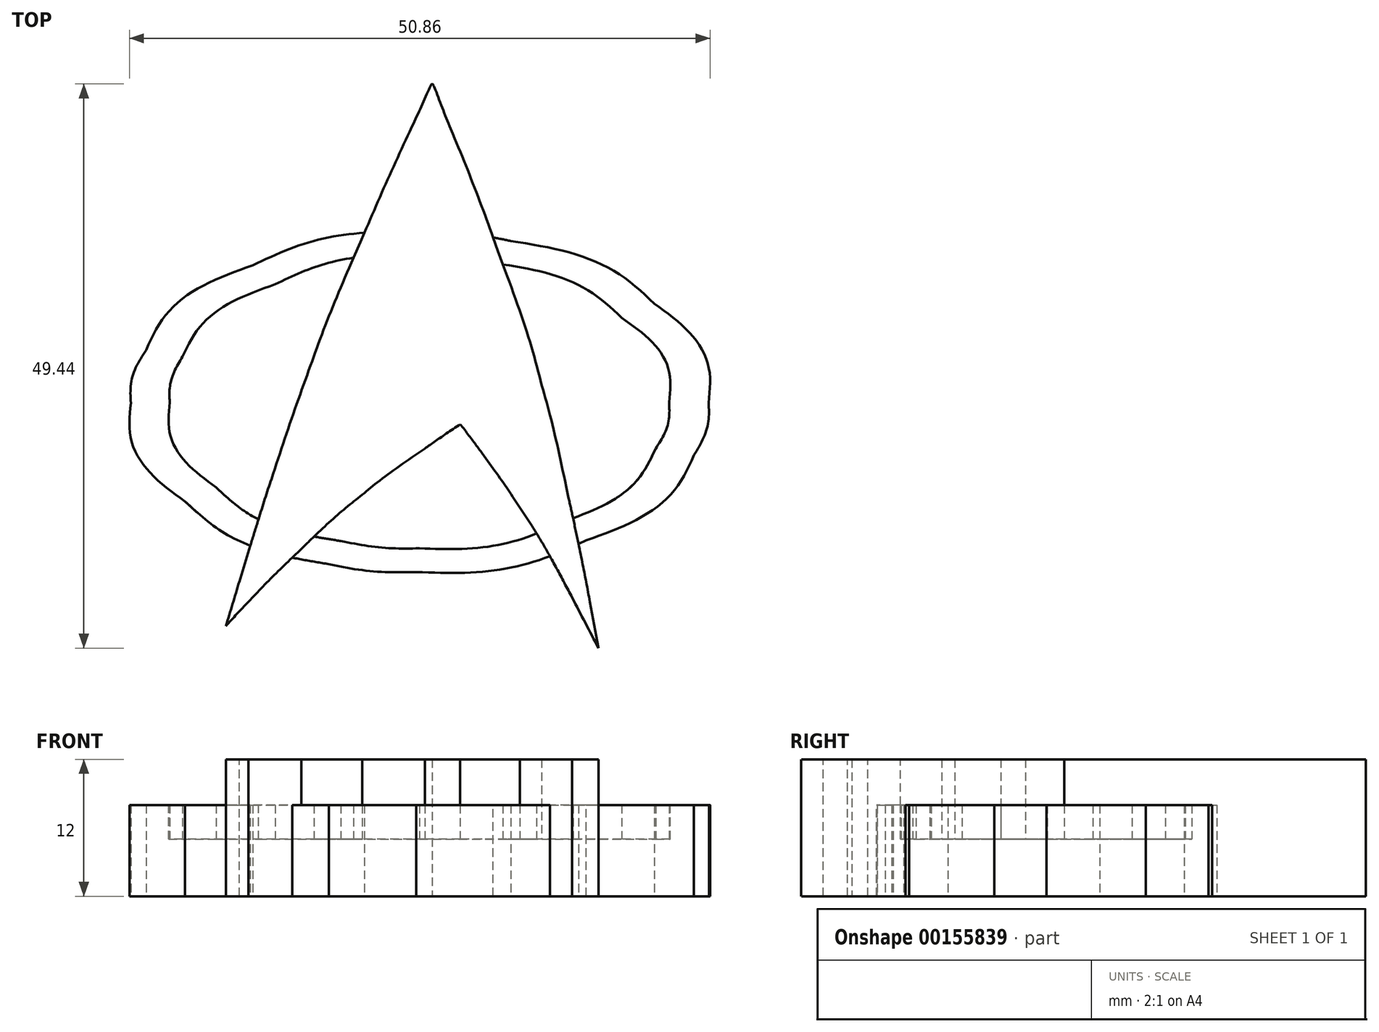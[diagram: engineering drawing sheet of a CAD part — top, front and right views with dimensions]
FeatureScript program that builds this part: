
annotation { "Feature Type Name" : "Feature", "Feature Type Description" : "" }
export const myFeature = defineFeature(function(context is Context, id is Id, definition is map)
    precondition{}
    {
        {
            var Q0;
            Q0=qCreatedBy(makeId("Top.planeOp"),FACE);
            var sketch = newSketch(context, id + "F0", { "sketchPlane" : qUnion([Q0])});
            skFitSpline(sketch, "E0", {"points": [v(14.01, -24.64) * mm, v(13.05, -22.8) * mm, v(12.29, -21.32) * mm, v(11.72, -20.22) * mm]});
            skFitSpline(sketch, "E1", {"points": [v(11.72, -20.22) * mm, v(9.94, -16.9) * mm, v(8.41, -14.28) * mm, v(7.13, -12.32) * mm]});
            skFitSpline(sketch, "E2", {"points": [v(7.13, -12.32) * mm, v(6.24, -10.97) * mm, v(5.14, -9.39) * mm, v(3.83, -7.58) * mm]});
            skFitSpline(sketch, "E3", {"points": [v(3.83, -7.58) * mm, v(3.36, -6.94) * mm, v(2.72, -6.08) * mm, v(1.9, -5.02) * mm]});
            skFitSpline(sketch, "E4", {"points": [v(1.9, -5.02) * mm, v(0.6, -5.9) * mm, v(-0.44, -6.62) * mm, v(-1.19, -7.15) * mm]});
            skFitSpline(sketch, "E5", {"points": [v(-1.19, -7.15) * mm, v(-3.64, -8.86) * mm, v(-5.47, -10.2) * mm, v(-6.68, -11.2) * mm]});
            skFitSpline(sketch, "E6", {"points": [v(-6.68, -11.2) * mm, v(-8.32, -12.52) * mm, v(-10.1, -14.1) * mm, v(-12.01, -15.95) * mm]});
            skFitSpline(sketch, "E7", {"points": [v(-12.01, -15.95) * mm, v(-13.68, -17.55) * mm, v(-15.23, -19.1) * mm, v(-16.65, -20.59) * mm]});
            skFitSpline(sketch, "E8", {"points": [v(-16.65, -20.59) * mm, v(-17.33, -21.3) * mm, v(-17.99, -22.01) * mm, v(-18.63, -22.72) * mm]});
            skFitSpline(sketch, "E9", {"points": [v(-18.63, -22.72) * mm, v(-18.24, -21.44) * mm, v(-17.84, -20.15) * mm, v(-17.45, -18.83) * mm]});
            skFitSpline(sketch, "E10", {"points": [v(-17.45, -18.83) * mm, v(-16.17, -14.67) * mm, v(-15.23, -11.67) * mm, v(-14.63, -9.82) * mm]});
            skFitSpline(sketch, "E11", {"points": [v(-14.63, -9.82) * mm, v(-13.49, -6.37) * mm, v(-12.35, -3.06) * mm, v(-11.21, 0.1) * mm]});
            skFitSpline(sketch, "E12", {"points": [v(-11.21, 0.1) * mm, v(-10.04, 3.3) * mm, v(-8.58, 6.91) * mm, v(-6.84, 10.93) * mm]});
            skFitSpline(sketch, "E13", {"points": [v(-6.84, 10.93) * mm, v(-5.42, 14.24) * mm, v(-3.98, 17.47) * mm, v(-2.52, 20.64) * mm]});
            skFitSpline(sketch, "E14", {"points": [v(-2.52, 20.64) * mm, v(-1.24, 23.41) * mm, v(-0.58, 24.8) * mm, v(-0.55, 24.8) * mm]});
            skFitSpline(sketch, "E15", {"points": [v(-0.55, 24.8) * mm, v(-0.51, 24.8) * mm, v(0.1, 23.34) * mm, v(1.27, 20.42) * mm]});
            skFitSpline(sketch, "E16", {"points": [v(1.27, 20.42) * mm, v(2.65, 17.01) * mm, v(3.97, 13.6) * mm, v(5.21, 10.18) * mm]});
            skFitSpline(sketch, "E17", {"points": [v(5.21, 10.18) * mm, v(6.92, 5.5) * mm, v(8.2, 1.56) * mm, v(9.05, -1.6) * mm]});
            skFitSpline(sketch, "E18", {"points": [v(9.05, -1.6) * mm, v(9.76, -4.2) * mm, v(10.55, -7.49) * mm, v(11.4, -11.47) * mm]});
            skFitSpline(sketch, "E19", {"points": [v(11.4, -11.47) * mm, v(12.11, -14.74) * mm, v(12.73, -17.78) * mm, v(13.27, -20.59) * mm]});
            skFitSpline(sketch, "E20", {"points": [v(13.27, -20.59) * mm, v(13.52, -21.94) * mm, v(13.76, -23.3) * mm, v(14.01, -24.64) * mm]});
            skFitSpline(sketch, "E21", {"points": [v(22.39, -7.74) * mm, v(20.64, -10.83) * mm, v(17.5, -13.32) * mm, v(12.95, -15.2) * mm]});
            skFitSpline(sketch, "E22", {"points": [v(12.95, -15.2) * mm, v(8.43, -17.05) * mm, v(3.47, -17.98) * mm, v(-1.93, -17.98) * mm]});
            skFitSpline(sketch, "E23", {"points": [v(-1.93, -17.98) * mm, v(-4.6, -17.98) * mm, v(-7.16, -17.75) * mm, v(-9.61, -17.28) * mm]});
            skFitSpline(sketch, "E24", {"points": [v(-9.61, -17.28) * mm, v(-14.84, -16.22) * mm, v(-19.04, -14.39) * mm, v(-22.2, -11.79) * mm]});
            skFitSpline(sketch, "E25", {"points": [v(-22.2, -11.79) * mm, v(-25.36, -9.16) * mm, v(-26.95, -6.28) * mm, v(-26.95, -3.15) * mm]});
            skFitSpline(sketch, "E26", {"points": [v(-26.95, -3.15) * mm, v(-26.95, -1.59) * mm, v(-26.5, -0.04) * mm, v(-25.61, 1.5) * mm]});
            skFitSpline(sketch, "E27", {"points": [v(-25.61, 1.5) * mm, v(-23.87, 4.58) * mm, v(-20.76, 7.05) * mm, v(-16.28, 8.9) * mm]});
            skFitSpline(sketch, "E28", {"points": [v(-16.28, 8.9) * mm, v(-11.8, 10.79) * mm, v(-6.86, 11.73) * mm, v(-1.45, 11.73) * mm]});
            skFitSpline(sketch, "E29", {"points": [v(-1.45, 11.73) * mm, v(1.28, 11.73) * mm, v(3.88, 11.5) * mm, v(6.33, 11.04) * mm]});
            skFitSpline(sketch, "E30", {"points": [v(6.33, 11.04) * mm, v(11.56, 10) * mm, v(15.76, 8.17) * mm, v(18.92, 5.54) * mm]});
            skFitSpline(sketch, "E31", {"points": [v(18.92, 5.54) * mm, v(22.08, 2.91) * mm, v(23.67, 0.01) * mm, v(23.67, -3.15) * mm]});
            skFitSpline(sketch, "E32", {"points": [v(23.67, -3.15) * mm, v(23.67, -4.64) * mm, v(23.24, -6.17) * mm, v(22.39, -7.74) * mm]});
            skFitSpline(sketch, "E33", {"points": [v(19.03, -7.15) * mm, v(19.8, -5.83) * mm, v(20.2, -4.48) * mm, v(20.2, -3.1) * mm]});
            skFitSpline(sketch, "E34", {"points": [v(20.2, -3.1) * mm, v(20.2, -0.4) * mm, v(18.81, 2.08) * mm, v(16.04, 4.32) * mm]});
            skFitSpline(sketch, "E35", {"points": [v(16.04, 4.32) * mm, v(13.3, 6.6) * mm, v(9.68, 8.17) * mm, v(5.16, 9.06) * mm]});
            skFitSpline(sketch, "E36", {"points": [v(5.16, 9.06) * mm, v(2.92, 9.5) * mm, v(0.66, 9.7) * mm, v(-1.61, 9.7) * mm]});
            skFitSpline(sketch, "E37", {"points": [v(-1.61, 9.7) * mm, v(-6.2, 9.7) * mm, v(-10.43, 8.89) * mm, v(-14.3, 7.25) * mm]});
            skFitSpline(sketch, "E38", {"points": [v(-14.3, 7.25) * mm, v(-18.18, 5.65) * mm, v(-20.88, 3.53) * mm, v(-22.41, 0.9) * mm]});
            skFitSpline(sketch, "E39", {"points": [v(-22.41, 0.9) * mm, v(-23.16, -0.45) * mm, v(-23.53, -1.78) * mm, v(-23.53, -3.1) * mm]});
            skFitSpline(sketch, "E40", {"points": [v(-23.53, -3.1) * mm, v(-23.53, -5.8) * mm, v(-22.18, -8.29) * mm, v(-19.48, -10.56) * mm]});
            skFitSpline(sketch, "E41", {"points": [v(-19.48, -10.56) * mm, v(-16.74, -12.8) * mm, v(-13.1, -14.37) * mm, v(-8.55, -15.26) * mm]});
            skFitSpline(sketch, "E42", {"points": [v(-8.55, -15.26) * mm, v(-6.24, -15.68) * mm, v(-3.94, -15.9) * mm, v(-1.67, -15.9) * mm]});
            skFitSpline(sketch, "E43", {"points": [v(-1.67, -15.9) * mm, v(2.96, -15.9) * mm, v(7.17, -15.11) * mm, v(10.97, -13.55) * mm]});
            skFitSpline(sketch, "E44", {"points": [v(10.97, -13.55) * mm, v(14.81, -11.95) * mm, v(17.5, -9.82) * mm, v(19.03, -7.15) * mm]});
            skSolve(sketch);
        }
        {
            var Q0;
            {var subQ4=sQuery(id+"F0.wireOp",EDGE,"E14");Q0=makeQuery(id+"F0.imprint","IMPRINT",FACE,{"disambiguationData":[TD([[makeQuery(id+"F0.imprint","IMPRINT",EDGE,{"derivedFrom":subQ4}),-1.0]])]});}
            var Q1;
            {var subQ12=sQuery(id+"F0.wireOp",EDGE,"E36");Q1=makeQuery(id+"F0.imprint","IMPRINT",FACE,{"disambiguationData":[TD([[makeQuery(id+"F0.imprint","IMPRINT",EDGE,{"derivedFrom":subQ12}),-1.0]])]});}
            var Q2;
            {var subQ17=sQuery(id+"F0.wireOp",EDGE,"E2");Q2=makeQuery(id+"F0.imprint","IMPRINT",FACE,{"disambiguationData":[TD([[makeQuery(id+"F0.imprint","IMPRINT",EDGE,{"derivedFrom":subQ17}),-1.0]])]});}
            var Q3;
            {var subQ1=sQuery(id+"F0.wireOp",EDGE,"E7");var subQ7=sQuery(id+"F0.wireOp",EDGE,"E6");var subQ8=makeQuery(id+"F0.imprint","INTERSECT",VERTEX,{"derivedFrom":[subQ7,subQ1]});Q3=makeQuery(id+"F0.imprint","IMPRINT",FACE,{"disambiguationData":[TD([[makeQuery(id+"F0.imprint","IMPRINT",EDGE,{"disambiguationData":[TD([[subQ8,1.0]])],"derivedFrom":subQ7}),-1.0]])]});}
            var Q4;
            {var subQ6=sQuery(id+"F0.wireOp",EDGE,"E8");Q4=makeQuery(id+"F0.imprint","IMPRINT",FACE,{"disambiguationData":[TD([[makeQuery(id+"F0.imprint","IMPRINT",EDGE,{"derivedFrom":subQ6}),-1.0]])]});}
            var Q5;
            {var subQ3=sQuery(id+"F0.wireOp",EDGE,"E1");var subQ5=sQuery(id+"F0.wireOp",EDGE,"E22");var subQ6=makeQuery(id+"F0.imprint","INTERSECT",VERTEX,{"derivedFrom":[subQ3,subQ5]});Q5=makeQuery(id+"F0.imprint","IMPRINT",FACE,{"disambiguationData":[TD([[makeQuery(id+"F0.imprint","IMPRINT",EDGE,{"disambiguationData":[TD([[subQ6,-1.0]])],"derivedFrom":subQ3}),-1.0]])]});}
            var Q6;
            {var subQ5=sQuery(id+"F0.wireOp",EDGE,"E0");Q6=makeQuery(id+"F0.imprint","IMPRINT",FACE,{"disambiguationData":[TD([[makeQuery(id+"F0.imprint","IMPRINT",EDGE,{"derivedFrom":subQ5}),-1.0]])]});}
            extrude(context, id + "F1", {"entities" : qUnion([Q0, Q1, Q2, Q3, Q4, Q5, Q6]), "depth" : 12 * mm});
        }
        {
            var Q0;
            {var subQ4=sQuery(id+"F0.wireOp",EDGE,"E25");Q0=makeQuery(id+"F0.imprint","IMPRINT",FACE,{"disambiguationData":[TD([[makeQuery(id+"F0.imprint","IMPRINT",EDGE,{"derivedFrom":subQ4}),-1.0]])]});}
            var Q1;
            {var subQ12=sQuery(id+"F0.wireOp",EDGE,"E36");Q1=makeQuery(id+"F0.imprint","IMPRINT",FACE,{"disambiguationData":[TD([[makeQuery(id+"F0.imprint","IMPRINT",EDGE,{"derivedFrom":subQ12}),-1.0]])]});}
            var Q2;
            {var subQ3=sQuery(id+"F0.wireOp",EDGE,"E21");Q2=makeQuery(id+"F0.imprint","IMPRINT",FACE,{"disambiguationData":[TD([[makeQuery(id+"F0.imprint","IMPRINT",EDGE,{"derivedFrom":subQ3}),-1.0]])]});}
            var Q3;
            {var subQ0=sQuery(id+"F0.wireOp",EDGE,"E23");Q3=makeQuery(id+"F0.imprint","IMPRINT",FACE,{"disambiguationData":[TD([[makeQuery(id+"F0.imprint","IMPRINT",EDGE,{"derivedFrom":subQ0}),-1.0]])]});}
            var Q4;
            {var subQ1=sQuery(id+"F0.wireOp",EDGE,"E7");var subQ7=sQuery(id+"F0.wireOp",EDGE,"E6");var subQ8=makeQuery(id+"F0.imprint","INTERSECT",VERTEX,{"derivedFrom":[subQ7,subQ1]});Q4=makeQuery(id+"F0.imprint","IMPRINT",FACE,{"disambiguationData":[TD([[makeQuery(id+"F0.imprint","IMPRINT",EDGE,{"disambiguationData":[TD([[subQ8,1.0]])],"derivedFrom":subQ7}),-1.0]])]});}
            var Q5;
            {var subQ3=sQuery(id+"F0.wireOp",EDGE,"E1");var subQ5=sQuery(id+"F0.wireOp",EDGE,"E22");var subQ6=makeQuery(id+"F0.imprint","INTERSECT",VERTEX,{"derivedFrom":[subQ3,subQ5]});Q5=makeQuery(id+"F0.imprint","IMPRINT",FACE,{"disambiguationData":[TD([[makeQuery(id+"F0.imprint","IMPRINT",EDGE,{"disambiguationData":[TD([[subQ6,-1.0]])],"derivedFrom":subQ3}),-1.0]])]});}
            extrude(context, id + "F2", {"entities" : qUnion([Q0, Q1, Q2, Q3, Q4, Q5]), "operationType" : NewBodyOperationType.ADD, "depth" : 8 * mm});
        }
        {
            var Q0;
            {var subQ4=sQuery(id+"F0.wireOp",EDGE,"E11");Q0=makeQuery(id+"F0.imprint","IMPRINT",FACE,{"disambiguationData":[TD([[makeQuery(id+"F0.imprint","IMPRINT",EDGE,{"derivedFrom":subQ4}),1.0]])]});}
            var Q1;
            {var subQ17=sQuery(id+"F0.wireOp",EDGE,"E2");Q1=makeQuery(id+"F0.imprint","IMPRINT",FACE,{"disambiguationData":[TD([[makeQuery(id+"F0.imprint","IMPRINT",EDGE,{"derivedFrom":subQ17}),-1.0]])]});}
            var Q2;
            {var subQ0=sQuery(id+"F0.wireOp",EDGE,"E2");Q2=makeQuery(id+"F0.imprint","IMPRINT",FACE,{"disambiguationData":[TD([[makeQuery(id+"F0.imprint","IMPRINT",EDGE,{"derivedFrom":subQ0}),1.0]])]});}
            var Q3;
            {var subQ1=sQuery(id+"F0.wireOp",EDGE,"E18");Q3=makeQuery(id+"F0.imprint","IMPRINT",FACE,{"disambiguationData":[TD([[makeQuery(id+"F0.imprint","IMPRINT",EDGE,{"derivedFrom":subQ1}),1.0]])]});}
            extrude(context, id + "F3", {"entities" : qUnion([Q0, Q1, Q2, Q3]), "operationType" : NewBodyOperationType.ADD, "depth" : 5 * mm});
        }
    });
